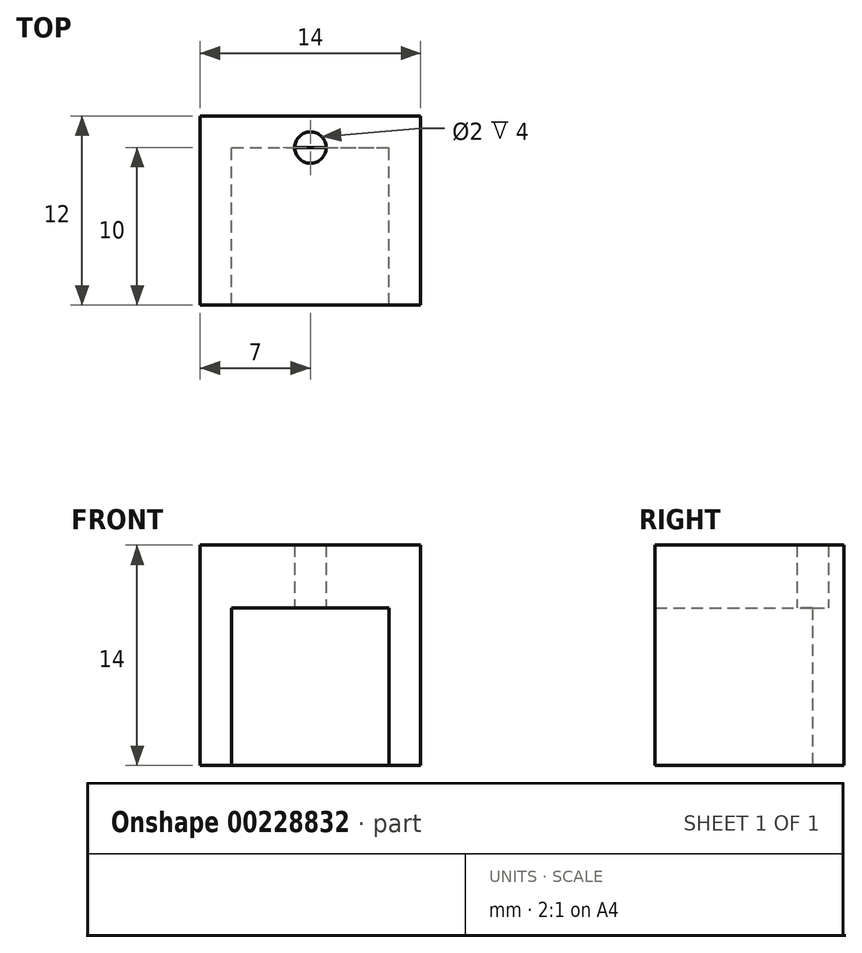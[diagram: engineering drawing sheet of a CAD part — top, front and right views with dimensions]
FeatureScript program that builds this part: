
annotation { "Feature Type Name" : "Feature", "Feature Type Description" : "" }
export const myFeature = defineFeature(function(context is Context, id is Id, definition is map)
    precondition{}
    {
        {
            var Q0;
            Q0=qCreatedBy(makeId("Top.planeOp"),FACE);
            var sketch = newSketch(context, id + "F0", { "sketchPlane" : qUnion([Q0])});
            skLineSegment(sketch, "E0.bottom", {"start": v(-7, 6) * mm, "end": v(7, 6) * mm});
            skLineSegment(sketch, "E0.top", {"start": v(-7, -6) * mm, "end": v(7, -6) * mm});
            skLineSegment(sketch, "E0.left", {"start": v(-7, 6) * mm, "end": v(-7, -6) * mm});
            skLineSegment(sketch, "E0.right", {"start": v(7, 6) * mm, "end": v(7, -6) * mm});
            skLineSegment(sketch, "E1.bottom", {"start": v(-5, -6) * mm, "end": v(5, -6) * mm});
            skLineSegment(sketch, "E1.top", {"start": v(-5, 4) * mm, "end": v(5, 4) * mm});
            skLineSegment(sketch, "E1.left", {"start": v(-5, -6) * mm, "end": v(-5, 4) * mm});
            skLineSegment(sketch, "E1.right", {"start": v(5, -6) * mm, "end": v(5, 4) * mm});
            skSolve(sketch);
        }
        {
            var Q0;
            Q0=makeQuery(id+"F0.imprint","IMPRINT",FACE,{"disambiguationData":[TD([[makeQuery(id+"F0.imprint","IMPRINT",EDGE,{"derivedFrom":sQuery(id+"F0.wireOp",EDGE,"E0.bottom")}),-1.0]])]});
            extrude(context, id + "F1", {"entities" : qUnion([Q0]), "depth" : 10 * mm});
        }
        {
            var Q0;
            Q0=makeQuery(id+"F1.opExtrude","CAP_FACE",FACE,{"disambiguationData":[OSD([sQuery(id+"F0.wireOp",EDGE,"E0.bottom"),sQuery(id+"F0.wireOp",EDGE,"E0.top"),sQuery(id+"F0.wireOp",EDGE,"E0.left"),sQuery(id+"F0.wireOp",EDGE,"E0.right"),sQuery(id+"F0.wireOp",EDGE,"E1.top"),sQuery(id+"F0.wireOp",EDGE,"E1.left"),sQuery(id+"F0.wireOp",EDGE,"E1.right")])],"isStart":false});
            var sketch = newSketch(context, id + "F2", { "sketchPlane" : qUnion([Q0])});
            skLineSegment(sketch, "E2.bottom", {"start": v(-7, 6) * mm, "end": v(7, 6) * mm});
            skLineSegment(sketch, "E2.top", {"start": v(-7, -6) * mm, "end": v(7, -6) * mm});
            skLineSegment(sketch, "E2.left", {"start": v(-7, 6) * mm, "end": v(-7, -6) * mm});
            skLineSegment(sketch, "E2.right", {"start": v(7, 6) * mm, "end": v(7, -6) * mm});
            skPoint(sketch, "E3", {"position": v(0, 4) * mm});
            skLineSegment(sketch, "E4", {"start": v(-7, 1.76) * mm, "end": v(7, 1.76) * mm});
            skSolve(sketch);
        }
        {
            var Q0;
            Q0 = qSketchRegion(id + "F2", true);
            extrude(context, id + "F3", {"entities" : qUnion([Q0]), "operationType" : NewBodyOperationType.ADD, "depth" : 4 * mm});
        }
        {
            var Q0;
            Q0=sQuery(id+"F2.wireOp",VERTEX,"E3");
            var Q1;
            Q1=makeQuery(id+"F1.opExtrude","SWEPT_BODY",BODY,{"disambiguationData":[OSD([sQuery(id+"F0.wireOp",EDGE,"E0.bottom"),sQuery(id+"F0.wireOp",EDGE,"E0.top"),sQuery(id+"F0.wireOp",EDGE,"E0.left"),sQuery(id+"F0.wireOp",EDGE,"E0.right"),sQuery(id+"F0.wireOp",EDGE,"E1.top"),sQuery(id+"F0.wireOp",EDGE,"E1.left"),sQuery(id+"F0.wireOp",EDGE,"E1.right")])]});
            hole(context, id + "F4", {"style" : HoleStyle.SIMPLE, "endStyle" : HoleEndStyle.THROUGH, "oppositeDirection" : true, "holeDiameter" : 2 * mm, "locations" : qUnion([Q0]), "scope" : qUnion([Q1]), "isTappedThrough" : true});
        }
    });
